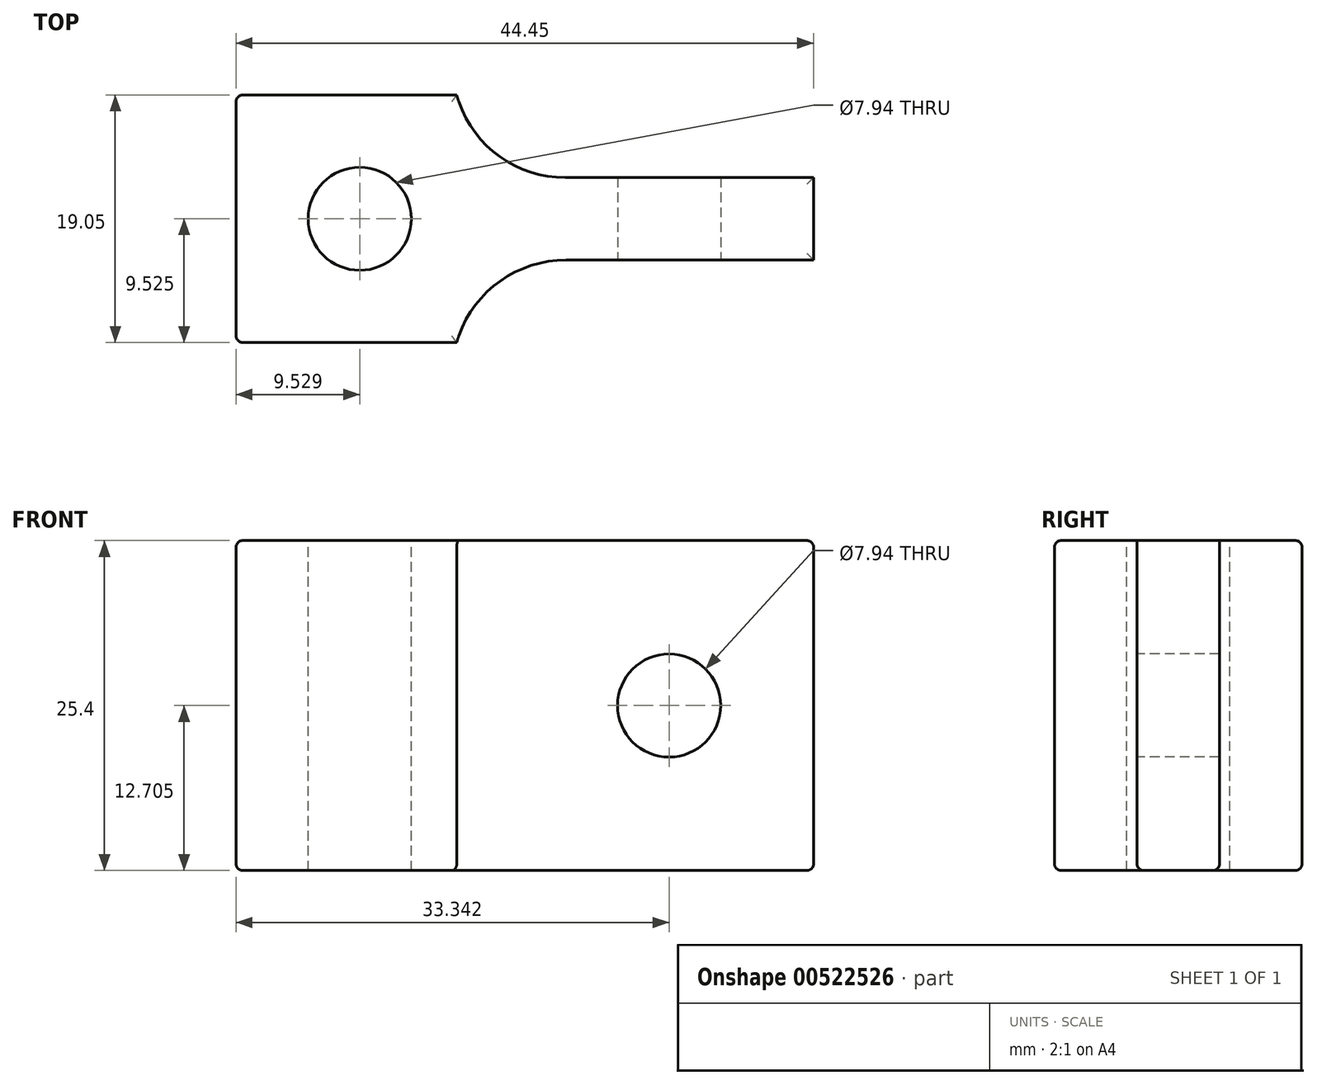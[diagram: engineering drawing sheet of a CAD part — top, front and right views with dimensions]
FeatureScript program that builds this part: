
annotation { "Feature Type Name" : "Feature", "Feature Type Description" : "" }
export const myFeature = defineFeature(function(context is Context, id is Id, definition is map)
    precondition{}
    {
        {
            var Q0;
            Q0=qCreatedBy(makeId("Front.planeOp"),FACE);
            var sketch = newSketch(context, id + "F0", { "sketchPlane" : qUnion([Q0])});
            skLineSegment(sketch, "E0.bottom", {"start": v(-16.99, 11.65) * mm, "end": v(27.46, 11.65) * mm});
            skLineSegment(sketch, "E0.top", {"start": v(-16.99, -13.75) * mm, "end": v(27.46, -13.75) * mm});
            skLineSegment(sketch, "E0.left", {"start": v(-16.99, 11.65) * mm, "end": v(-16.99, -13.75) * mm});
            skLineSegment(sketch, "E0.right", {"start": v(27.46, 11.65) * mm, "end": v(27.46, -13.75) * mm});
            skSolve(sketch);
        }
        {
            var Q0;
            Q0=makeQuery(id+"F0.imprint","IMPRINT",FACE,{"disambiguationData":[TD([[makeQuery(id+"F0.imprint","IMPRINT",EDGE,{"derivedFrom":sQuery(id+"F0.wireOp",EDGE,"E0.bottom")}),-1.0]])]});
            extrude(context, id + "F1", {"entities" : qUnion([Q0]), "depth" : 19.05 * mm, "offsetDistance" : 25.4 * mm});
        }
        {
            var Q0;
            Q0=makeQuery(id+"F1.opExtrude","SWEPT_FACE",FACE,{"disambiguationData":[OSD([sQuery(id+"F0.wireOp",EDGE,"E0.bottom")])]});
            var sketch = newSketch(context, id + "F2", { "sketchPlane" : qUnion([Q0])});
            skCircle(sketch, "E1", {"center": v(-7.46, -9.53) * mm, "radius": 3.97 * mm});
            skLineSegment(sketch, "E2", {"start": v(-16.99, -9.53) * mm, "end": v(-7.46, -9.53) * mm, "construction": true});
            skPoint(sketch, "E2.endSnap0", {"position": v(-16.99, -9.53) * mm});
            skSolve(sketch);
        }
        {
            var Q0;
            Q0 = qSketchRegion(id + "F2", true);
            var Q1;
            Q1=makeQuery(id+"F1.opExtrude","SWEPT_FACE",FACE,{"disambiguationData":[OSD([sQuery(id+"F0.wireOp",EDGE,"E0.top")])]});
            extrude(context, id + "F3", {"entities" : qUnion([Q0]), "operationType" : NewBodyOperationType.REMOVE, "endBound" : BoundingType.UP_TO_SURFACE, "oppositeDirection" : true, "depth" : 25.4 * mm, "endBoundEntityFace" : qUnion([Q1]), "offsetDistance" : 25.4 * mm});
        }
        {
            var Q0;
            Q0=makeQuery(id+"F1.opExtrude","CAP_FACE",FACE,{"disambiguationData":[OSD([sQuery(id+"F0.wireOp",EDGE,"E0.bottom"),sQuery(id+"F0.wireOp",EDGE,"E0.top"),sQuery(id+"F0.wireOp",EDGE,"E0.left"),sQuery(id+"F0.wireOp",EDGE,"E0.right")])],"isStart":false});
            var sketch = newSketch(context, id + "F4", { "sketchPlane" : qUnion([Q0])});
            skCircle(sketch, "E3", {"center": v(16.35, -1.05) * mm, "radius": 3.97 * mm});
            skLineSegment(sketch, "E4", {"start": v(27.46, -1.05) * mm, "end": v(16.35, -1.05) * mm, "construction": true});
            skLineSegment(sketch, "E5", {"start": v(16.35, -1.05) * mm, "end": v(16.35, -13.75) * mm});
            skSolve(sketch);
        }
        {
            var Q0;
            Q0=makeQuery(id+"F4.imprint","IMPRINT",FACE,{"disambiguationData":[TD([[makeQuery(id+"F4.imprint","IMPRINT",EDGE,{"derivedFrom":sQuery(id+"F4.wireOp",EDGE,"E3")}),1.0]])]});
            var Q1;
            Q1=makeQuery(id+"F1.opExtrude","CAP_FACE",FACE,{"disambiguationData":[OSD([sQuery(id+"F0.wireOp",EDGE,"E0.bottom"),sQuery(id+"F0.wireOp",EDGE,"E0.top"),sQuery(id+"F0.wireOp",EDGE,"E0.left"),sQuery(id+"F0.wireOp",EDGE,"E0.right")])],"isStart":true});
            extrude(context, id + "F5", {"entities" : qUnion([Q0]), "operationType" : NewBodyOperationType.REMOVE, "endBound" : BoundingType.UP_TO_SURFACE, "oppositeDirection" : true, "depth" : 25.4 * mm, "endBoundEntityFace" : qUnion([Q1]), "offsetDistance" : 25.4 * mm});
        }
        {
            var Q0;
            Q0=makeQuery(id+"F1.opExtrude","SWEPT_EDGE",EDGE,{"disambiguationData":[OSD([sQuery(id+"F0.wireOp",EDGE,"E0.bottom"),sQuery(id+"F0.wireOp",EDGE,"E0.left")])]});
            var Q1;
            Q1=makeQuery(id+"F1.opExtrude","CAP_EDGE",EDGE,{"disambiguationData":[OSD([sQuery(id+"F0.wireOp",EDGE,"E0.bottom")])],"isStart":false});
            var Q2;
            Q2=makeQuery(id+"F1.opExtrude","SWEPT_EDGE",EDGE,{"disambiguationData":[OSD([sQuery(id+"F0.wireOp",EDGE,"E0.bottom"),sQuery(id+"F0.wireOp",EDGE,"E0.right")])]});
            var Q3;
            Q3=makeQuery(id+"F1.opExtrude","CAP_EDGE",EDGE,{"disambiguationData":[OSD([sQuery(id+"F0.wireOp",EDGE,"E0.bottom")])],"isStart":true});
            fillet(context, id + "F6", {"entities" : qUnion([Q0, Q1, Q2, Q3]), "radius" : 0.5 * mm, "tangentPropagation" : true, "allowEdgeOverflow" : false});
        }
        {
            var Q0;
            Q0=makeQuery(id+"F2.imprint","IMPRINT",FACE,{"disambiguationData":[TD([[makeQuery(id+"F2.imprint","IMPRINT",EDGE,{"derivedFrom":sQuery(id+"F2.wireOp",EDGE,"E1")}),-1.0]])]});
            var sketch = newSketch(context, id + "F7", { "sketchPlane" : qUnion([Q0])});
            skLineSegment(sketch, "E6", {"start": v(27.4, -12.7) * mm, "end": v(8.35, -12.7) * mm, "construction": true});
            skLineSegment(sketch, "E7", {"start": v(8.35, -6.35) * mm, "end": v(27.64, -6.35) * mm});
            skLineSegment(sketch, "E8", {"start": v(19.91, -19.05) * mm, "end": v(19.91, -12.7) * mm, "construction": true});
            skArc(sketch, "E9", {"start": v(0, 0) * mm, "mid": v(3.1, -4.58) * mm, "end": v(8.35, -6.35) * mm});
            skArc(sketch, "E10", {"start": v(8.35, -12.7) * mm, "mid": v(3.12, -14.45) * mm, "end": v(0, -19) * mm, "construction": true});
            skSolve(sketch);
        }
        {
            var Q0;
            {var subQ0=sQuery(id+"F7.wireOp",EDGE,"E9");Q0=makeQuery(id+"F7.imprint","IMPRINT",FACE,{"disambiguationData":[TD([[makeQuery(id+"F7.imprint","IMPRINT",EDGE,{"derivedFrom":subQ0}),1.0]])]});}
            extrude(context, id + "F8", {"entities" : qUnion([Q0]), "operationType" : NewBodyOperationType.REMOVE, "endBound" : BoundingType.THROUGH_ALL, "oppositeDirection" : true, "depth" : 25.4 * mm, "offsetDistance" : 25.4 * mm});
        }
        {
            var Q0;
            Q0=makeQuery(id+"F2.imprint","IMPRINT",FACE,{"disambiguationData":[TD([[makeQuery(id+"F2.imprint","IMPRINT",EDGE,{"derivedFrom":sQuery(id+"F2.wireOp",EDGE,"E1")}),-1.0]])]});
            var sketch = newSketch(context, id + "F9", { "sketchPlane" : qUnion([Q0])});
            skLineSegment(sketch, "E11", {"start": v(27.46, -12.7) * mm, "end": v(8.41, -12.7) * mm});
            skLineSegment(sketch, "E12", {"start": v(22.78, -12.7) * mm, "end": v(22.78, -19.05) * mm, "construction": true});
            skArc(sketch, "E13", {"start": v(8.41, -12.7) * mm, "mid": v(3.14, -14.47) * mm, "end": v(0, -19.05) * mm});
            skSolve(sketch);
        }
        {
            var Q0;
            {var subQ0=sQuery(id+"F9.wireOp",EDGE,"E11");Q0=makeQuery(id+"F9.imprint","IMPRINT",FACE,{"disambiguationData":[TD([[makeQuery(id+"F9.imprint","IMPRINT",EDGE,{"derivedFrom":subQ0}),1.0]])]});}
            extrude(context, id + "F10", {"entities" : qUnion([Q0]), "operationType" : NewBodyOperationType.REMOVE, "endBound" : BoundingType.THROUGH_ALL, "oppositeDirection" : true, "depth" : 25.4 * mm, "offsetDistance" : 25.4 * mm});
        }
        {
            var Q0;
            Q0=makeQuery(id+"F10.boolean.opBoolean","COPY",EDGE,{"derivedFrom":makeQuery(id+"F10.opExtrude","CAP_EDGE",EDGE,{"disambiguationData":[OSD([sQuery(id+"F9.wireOp",EDGE,"E13")])],"isStart":true})});
            var Q1;
            Q1=makeQuery(id+"F8.boolean.opBoolean","COPY",EDGE,{"derivedFrom":makeQuery(id+"F8.opExtrude","CAP_EDGE",EDGE,{"disambiguationData":[OSD([sQuery(id+"F7.wireOp",EDGE,"E9")])],"isStart":true})});
            var Q2;
            Q2=makeQuery(id+"F8.boolean.opBoolean","COPY",EDGE,{"derivedFrom":makeQuery(id+"F8.opExtrude","CAP_EDGE",EDGE,{"disambiguationData":[OSD([sQuery(id+"F7.wireOp",EDGE,"E7")])],"isStart":true})});
            var Q3;
            Q3=makeQuery(id+"F1.opExtrude","CAP_EDGE",EDGE,{"disambiguationData":[OSD([sQuery(id+"F0.wireOp",EDGE,"E0.left")])],"isStart":false});
            var Q4;
            Q4=makeQuery(id+"F1.opExtrude","CAP_EDGE",EDGE,{"disambiguationData":[OSD([sQuery(id+"F0.wireOp",EDGE,"E0.left")])],"isStart":true});
            var Q5;
            Q5=makeQuery(id+"F1.opExtrude","SWEPT_EDGE",EDGE,{"disambiguationData":[OSD([sQuery(id+"F0.wireOp",EDGE,"E0.top"),sQuery(id+"F0.wireOp",EDGE,"E0.left")])]});
            var Q6;
            Q6=makeQuery(id+"F10.boolean.opBoolean","COPY",EDGE,{"derivedFrom":makeQuery(id+"F10.opExtrude","SWEPT_EDGE",EDGE,{"disambiguationData":[OSD([sQuery(id+"F0.wireOp",EDGE,"E0.bottom"),sQuery(id+"F9.wireOp",EDGE,"E13")])]})});
            var Q7;
            Q7=makeQuery(id+"F10.boolean.opBoolean","COPY",EDGE,{"derivedFrom":makeQuery(id+"F10.opExtrude","SWEPT_EDGE",EDGE,{"disambiguationData":[OSD([sQuery(id+"F0.wireOp",EDGE,"E0.bottom"),sQuery(id+"F0.wireOp",EDGE,"E0.right"),sQuery(id+"F9.wireOp",EDGE,"E11")])]})});
            var Q8;
            Q8=makeQuery(id+"F10.boolean.opBoolean","INTERSECT",EDGE,{"derivedFrom":[makeQuery(id+"F1.opExtrude","SWEPT_FACE",FACE,{"disambiguationData":[OSD([sQuery(id+"F0.wireOp",EDGE,"E0.top")])]}),makeQuery(id+"F10.opExtrude","SWEPT_FACE",FACE,{"disambiguationData":[OSD([sQuery(id+"F9.wireOp",EDGE,"E13")])]})]});
            var Q9;
            Q9=makeQuery(id+"F10.boolean.opBoolean","INTERSECT",EDGE,{"derivedFrom":[makeQuery(id+"F1.opExtrude","SWEPT_FACE",FACE,{"disambiguationData":[OSD([sQuery(id+"F0.wireOp",EDGE,"E0.top")])]}),makeQuery(id+"F10.opExtrude","SWEPT_FACE",FACE,{"disambiguationData":[OSD([sQuery(id+"F9.wireOp",EDGE,"E11")])]})]});
            var Q10;
            Q10=makeQuery(id+"F1.opExtrude","CAP_EDGE",EDGE,{"disambiguationData":[OSD([sQuery(id+"F0.wireOp",EDGE,"E0.top")])],"isStart":false});
            var Q11;
            Q11=makeQuery(id+"F1.opExtrude","CAP_EDGE",EDGE,{"disambiguationData":[OSD([sQuery(id+"F0.wireOp",EDGE,"E0.top")])],"isStart":true});
            var Q12;
            Q12=makeQuery(id+"F8.boolean.opBoolean","COPY",EDGE,{"derivedFrom":makeQuery(id+"F8.opExtrude","SWEPT_EDGE",EDGE,{"disambiguationData":[OSD([sQuery(id+"F0.wireOp",EDGE,"E0.bottom"),sQuery(id+"F7.wireOp",EDGE,"E9")])]})});
            var Q13;
            Q13=makeQuery(id+"F8.boolean.opBoolean","INTERSECT",EDGE,{"derivedFrom":[makeQuery(id+"F1.opExtrude","SWEPT_FACE",FACE,{"disambiguationData":[OSD([sQuery(id+"F0.wireOp",EDGE,"E0.top")])]}),makeQuery(id+"F8.opExtrude","SWEPT_FACE",FACE,{"disambiguationData":[OSD([sQuery(id+"F7.wireOp",EDGE,"E9")])]})]});
            var Q14;
            Q14=makeQuery(id+"F8.boolean.opBoolean","INTERSECT",EDGE,{"derivedFrom":[makeQuery(id+"F1.opExtrude","SWEPT_FACE",FACE,{"disambiguationData":[OSD([sQuery(id+"F0.wireOp",EDGE,"E0.top")])]}),makeQuery(id+"F8.opExtrude","SWEPT_FACE",FACE,{"disambiguationData":[OSD([sQuery(id+"F7.wireOp",EDGE,"E7")])]})]});
            var Q15;
            Q15=makeQuery(id+"F1.opExtrude","SWEPT_EDGE",EDGE,{"disambiguationData":[OSD([sQuery(id+"F0.wireOp",EDGE,"E0.top"),sQuery(id+"F0.wireOp",EDGE,"E0.right")])]});
            fillet(context, id + "F11", {"entities" : qUnion([Q0, Q1, Q2, Q3, Q4, Q5, Q6, Q7, Q8, Q9, Q10, Q11, Q12, Q13, Q14, Q15]), "radius" : 0.5 * mm, "tangentPropagation" : true, "allowEdgeOverflow" : false});
        }
    });
